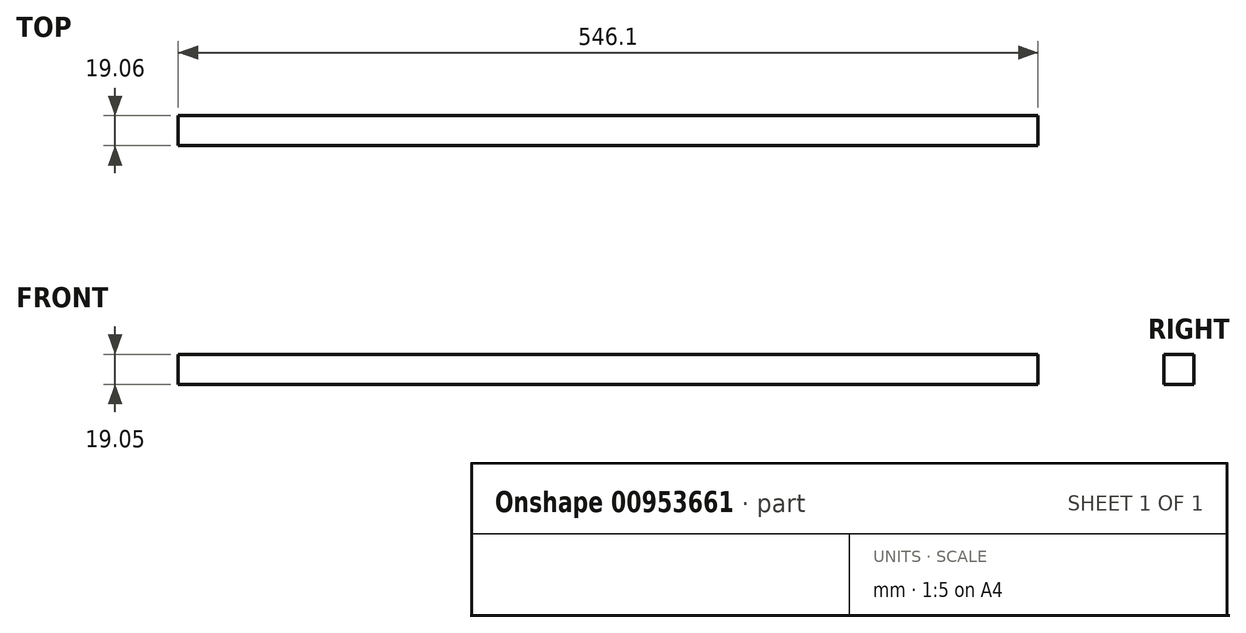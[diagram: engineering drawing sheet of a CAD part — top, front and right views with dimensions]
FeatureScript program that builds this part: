
annotation { "Feature Type Name" : "Feature", "Feature Type Description" : "" }
export const myFeature = defineFeature(function(context is Context, id is Id, definition is map)
    precondition{}
    {
        {
            var Q0;
            Q0=qCreatedBy(makeId("Top.planeOp"),FACE);
            var sketch = newSketch(context, id + "F0", { "sketchPlane" : qUnion([Q0])});
            skLineSegment(sketch, "E0.bottom", {"start": v(273.05, -9.52) * mm, "end": v(-273.05, -9.53) * mm});
            skLineSegment(sketch, "E0.top", {"start": v(273.05, 9.53) * mm, "end": v(-273.05, 9.52) * mm});
            skLineSegment(sketch, "E0.left", {"start": v(273.05, -9.52) * mm, "end": v(273.05, 9.53) * mm});
            skLineSegment(sketch, "E0.right", {"start": v(-273.05, -9.53) * mm, "end": v(-273.05, 9.52) * mm});
            skPoint(sketch, "E0.middle", {"position": v(0, 0) * mm});
            skSolve(sketch);
        }
        {
            var Q0;
            Q0=makeQuery(id+"F0.imprint","IMPRINT",FACE,{"disambiguationData":[TD([[makeQuery(id+"F0.imprint","IMPRINT",EDGE,{"derivedFrom":sQuery(id+"F0.wireOp",EDGE,"E0.bottom")}),-1.0]])]});
            extrude(context, id + "F1", {"entities" : qUnion([Q0]), "depth" : 19.05 * mm, "offsetDistance" : 25.4 * mm});
        }
    });
